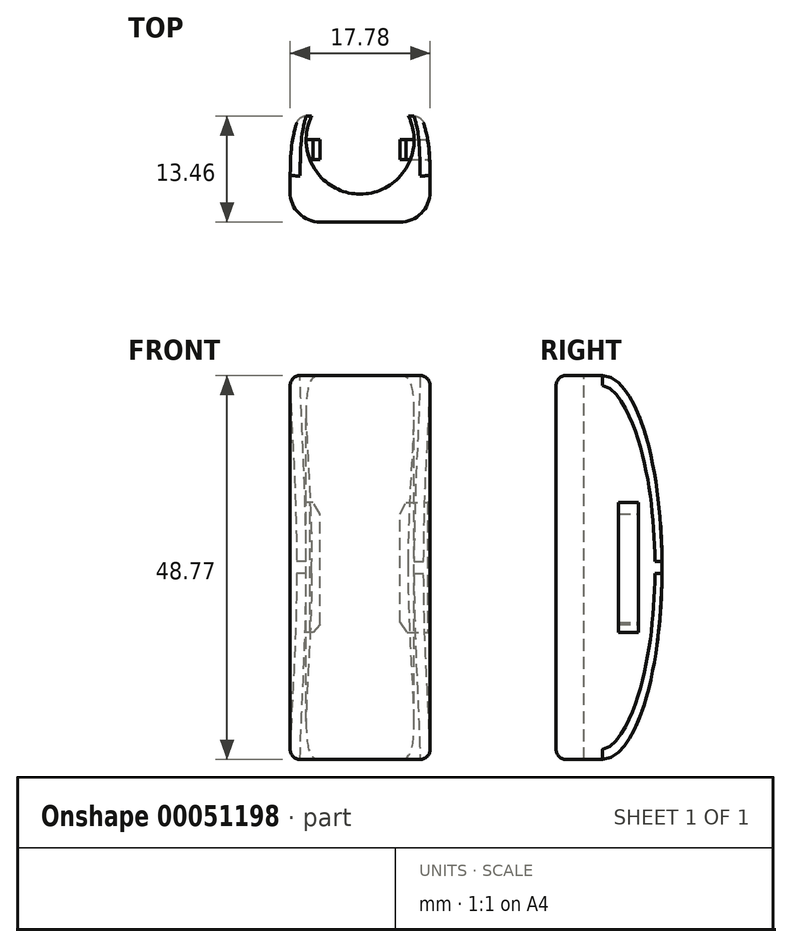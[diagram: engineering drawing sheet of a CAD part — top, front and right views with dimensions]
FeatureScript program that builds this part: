
annotation { "Feature Type Name" : "Feature", "Feature Type Description" : "" }
export const myFeature = defineFeature(function(context is Context, id is Id, definition is map)
    precondition{}
    {
        {
            var Q0;
            Q0=qCreatedBy(makeId("Top.planeOp"),FACE);
            var sketch = newSketch(context, id + "F0", { "sketchPlane" : qUnion([Q0])});
            skLineSegment(sketch, "E0.bottom", {"start": v(-25.3, 22.65) * mm, "end": v(-7.52, 22.65) * mm});
            skLineSegment(sketch, "E0.top", {"start": v(-25.3, 9.19) * mm, "end": v(-7.52, 9.19) * mm});
            skLineSegment(sketch, "E0.left", {"start": v(-25.3, 22.65) * mm, "end": v(-25.3, 9.19) * mm});
            skLineSegment(sketch, "E0.right", {"start": v(-7.52, 22.65) * mm, "end": v(-7.52, 9.19) * mm});
            skSolve(sketch);
        }
        {
            var Q0;
            Q0=makeQuery(id+"F0.imprint","IMPRINT",FACE,{"disambiguationData":[TD([[makeQuery(id+"F0.imprint","IMPRINT",EDGE,{"derivedFrom":sQuery(id+"F0.wireOp",EDGE,"E0.bottom")}),-1.0]])]});
            extrude(context, id + "F1", {"entities" : qUnion([Q0]), "depth" : 48.77 * mm});
        }
        {
            var Q0;
            Q0=makeQuery(id+"F1.opExtrude","CAP_FACE",FACE,{"disambiguationData":[OSD([sQuery(id+"F0.wireOp",EDGE,"E0.bottom"),sQuery(id+"F0.wireOp",EDGE,"E0.top"),sQuery(id+"F0.wireOp",EDGE,"E0.left"),sQuery(id+"F0.wireOp",EDGE,"E0.right")])],"isStart":false});
            var sketch = newSketch(context, id + "F2", { "sketchPlane" : qUnion([Q0])});
            skCircle(sketch, "E1", {"center": v(-16.41, 19.6) * mm, "radius": 6.86 * mm});
            skSolve(sketch);
        }
        {
            var Q0;
            {var subQ0=sQuery(id+"F2.wireOp",EDGE,"E1");var subQ1=makeQuery(id+"F1.opExtrude","CAP_EDGE",EDGE,{"disambiguationData":[OSD([sQuery(id+"F0.wireOp",EDGE,"E0.bottom")])],"isStart":false});var subQ2=makeQuery(id+"F2.imprint","INTERSECT",VERTEX,{"disambiguationData":[OD(0.0)],"derivedFrom":[subQ1,subQ0]});Q0=makeQuery(id+"F2.imprint","IMPRINT",FACE,{"disambiguationData":[TD([[makeQuery(id+"F2.imprint","IMPRINT",EDGE,{"disambiguationData":[TD([[subQ2,1.0]])],"derivedFrom":subQ0}),1.0]])]});}
            var Q1;
            {var subQ0=sQuery(id+"F2.wireOp",EDGE,"E1");var subQ1=makeQuery(id+"F1.opExtrude","CAP_EDGE",EDGE,{"disambiguationData":[OSD([sQuery(id+"F0.wireOp",EDGE,"E0.bottom")])],"isStart":false});var subQ2=makeQuery(id+"F2.imprint","INTERSECT",VERTEX,{"disambiguationData":[OD(0.0)],"derivedFrom":[subQ1,subQ0]});Q1=makeQuery(id+"F2.imprint","IMPRINT",FACE,{"disambiguationData":[TD([[makeQuery(id+"F2.imprint","IMPRINT",EDGE,{"disambiguationData":[TD([[subQ2,-1.0]])],"derivedFrom":subQ0}),1.0]])]});}
            extrude(context, id + "F3", {"entities" : qUnion([Q0, Q1]), "operationType" : NewBodyOperationType.REMOVE, "oppositeDirection" : true, "depth" : 127 * mm});
        }
        {
            var Q0;
            Q0=makeQuery(id+"F1.opExtrude","SWEPT_FACE",FACE,{"disambiguationData":[OSD([sQuery(id+"F0.wireOp",EDGE,"E0.left")])]});
            var sketch = newSketch(context, id + "F4", { "sketchPlane" : qUnion([Q0])});
            skLineSegment(sketch, "E2.bottom", {"start": v(-19.66, 16.13) * mm, "end": v(-17.12, 16.13) * mm});
            skLineSegment(sketch, "E2.top", {"start": v(-19.66, 32.64) * mm, "end": v(-17.12, 32.64) * mm});
            skLineSegment(sketch, "E2.left", {"start": v(-19.66, 16.13) * mm, "end": v(-19.66, 32.64) * mm});
            skLineSegment(sketch, "E2.right", {"start": v(-17.12, 16.13) * mm, "end": v(-17.12, 32.64) * mm});
            skSolve(sketch);
        }
        {
            var Q0;
            Q0=makeQuery(id+"F4.imprint","IMPRINT",FACE,{"disambiguationData":[TD([[makeQuery(id+"F4.imprint","IMPRINT",EDGE,{"derivedFrom":sQuery(id+"F4.wireOp",EDGE,"E2.bottom")}),1.0]])]});
            extrude(context, id + "F5", {"entities" : qUnion([Q0]), "operationType" : NewBodyOperationType.ADD, "oppositeDirection" : true, "depth" : 3.8 * mm});
        }
        {
            var Q0;
            Q0=makeQuery(id+"F1.opExtrude","CAP_FACE",FACE,{"disambiguationData":[OSD([sQuery(id+"F0.wireOp",EDGE,"E0.bottom"),sQuery(id+"F0.wireOp",EDGE,"E0.top"),sQuery(id+"F0.wireOp",EDGE,"E0.left"),sQuery(id+"F0.wireOp",EDGE,"E0.right")])],"isStart":false});
            var sketch = newSketch(context, id + "F6", { "sketchPlane" : qUnion([Q0])});
            skFitSpline(sketch, "E3", {"points": [v(-25.3, 12.21) * mm, v(-25.07, 19.12) * mm, v(-24.21, 22.65) * mm], "startDerivative": vector(-0.07, 12.93) * mm, "endDerivative": vector(2.38, 7.66) * mm});
            skFitSpline(sketch, "E4.MirrorCS", {"points": [v(-7.52, 12.21) * mm, v(-7.76, 19.12) * mm, v(-8.61, 22.65) * mm], "startDerivative": vector(0.07, 12.93) * mm, "endDerivative": vector(-2.38, 7.66) * mm});
            skSolve(sketch);
        }
        {
            var Q0;
            {var subQ0=sQuery(id+"F6.wireOp",EDGE,"fc3628cf-69c2-4551-9983-d84b999a87e0");Q0=makeQuery(id+"F6.imprint","IMPRINT",FACE,{"disambiguationData":[TD([[makeQuery(id+"F6.imprint","IMPRINT",EDGE,{"derivedFrom":subQ0}),1.0]])]});}
            var Q1;
            {var subQ0=sQuery(id+"F6.wireOp",EDGE,"20fc23eb-cc5c-43b9-b7d9-6a3f5bb52c0f0.MirrorCS");Q1=makeQuery(id+"F6.imprint","IMPRINT",FACE,{"disambiguationData":[TD([[makeQuery(id+"F6.imprint","IMPRINT",EDGE,{"derivedFrom":subQ0}),-1.0]])]});}
            var Q2;
            {var subQ0=sQuery(id+"F6.wireOp",EDGE,"E3");var subQ2=sQuery(id+"F0.wireOp",EDGE,"E0.left");var subQ5=makeQuery(id+"F1.opExtrude","CAP_EDGE",EDGE,{"disambiguationData":[OSD([subQ2])],"isStart":false});var subQ6=makeQuery(id+"F6.imprint","INTERSECT",VERTEX,{"disambiguationData":[OD(1.0)],"derivedFrom":[subQ5,subQ0]});Q2=makeQuery(id+"F6.imprint","IMPRINT",FACE,{"disambiguationData":[TD([[makeQuery(id+"F6.imprint","IMPRINT",EDGE,{"disambiguationData":[TD([[subQ6,-1.0]])],"derivedFrom":subQ0}),1.0]])]});}
            var Q3;
            {var subQ0=sQuery(id+"F6.wireOp",EDGE,"E4.MirrorCS");var subQ2=sQuery(id+"F0.wireOp",EDGE,"E0.right");var subQ5=makeQuery(id+"F1.opExtrude","CAP_EDGE",EDGE,{"disambiguationData":[OSD([subQ2])],"isStart":false});var subQ6=makeQuery(id+"F6.imprint","INTERSECT",VERTEX,{"disambiguationData":[OD(1.0)],"derivedFrom":[subQ5,subQ0]});Q3=makeQuery(id+"F6.imprint","IMPRINT",FACE,{"disambiguationData":[TD([[makeQuery(id+"F6.imprint","IMPRINT",EDGE,{"disambiguationData":[TD([[subQ6,-1.0]])],"derivedFrom":subQ0}),-1.0]])]});}
            extrude(context, id + "F7", {"entities" : qUnion([Q0, Q1, Q2, Q3]), "operationType" : NewBodyOperationType.REMOVE, "oppositeDirection" : true, "depth" : 76.2 * mm});
        }
        {
            var Q0;
            Q0=makeQuery(id+"F1.opExtrude","SWEPT_EDGE",EDGE,{"disambiguationData":[OSD([sQuery(id+"F0.wireOp",EDGE,"E0.top"),sQuery(id+"F0.wireOp",EDGE,"E0.right")])]});
            var Q1;
            Q1=makeQuery(id+"F1.opExtrude","SWEPT_EDGE",EDGE,{"disambiguationData":[OSD([sQuery(id+"F0.wireOp",EDGE,"E0.top"),sQuery(id+"F0.wireOp",EDGE,"E0.left")])]});
            fillet(context, id + "F8", {"entities" : qUnion([Q0, Q1]), "radius" : 3.8 * mm, "tangentPropagation" : true, "allowEdgeOverflow" : false});
        }
        {
            var Q0;
            Q0=makeQuery(id+"F1.opExtrude","SWEPT_FACE",FACE,{"disambiguationData":[OSD([sQuery(id+"F0.wireOp",EDGE,"E0.left")])]});
            var sketch = newSketch(context, id + "F9", { "sketchPlane" : qUnion([Q0])});
            skEllipticalArc(sketch, "E5", {});
            skLineSegment(sketch, "E6", {"start": v(-15.06, 0) * mm, "end": v(-22.79, -10.05) * mm});
            skLineSegment(sketch, "E7", {"start": v(-22.79, -10.05) * mm, "end": v(-30.31, 18.86) * mm});
            skLineSegment(sketch, "E8", {"start": v(-30.31, 18.86) * mm, "end": v(-22.65, 24.38) * mm});
            skLineSegment(sketch, "E9", {"start": v(-22.65, 24.38) * mm, "end": v(-30.46, 41.8) * mm});
            skLineSegment(sketch, "E10", {"start": v(-30.46, 41.8) * mm, "end": v(-18.14, 61.05) * mm});
            skLineSegment(sketch, "E11", {"start": v(-18.14, 61.05) * mm, "end": v(-15.06, 48.77) * mm});
            const initialGuessF9  = {"E5": [-0.015061341374097393, 0.024384, 0, 1, 0.024384, 0.0075914439429358585, 0, 3.141592653589793]};
            skSetInitialGuess(sketch, initialGuessF9);
            skSolve(sketch);
        }
        {
            var Q0;
            {var subQ0=sQuery(id+"F9.wireOp",EDGE,"E6");Q0=makeQuery(id+"F9.imprint","IMPRINT",FACE,{"disambiguationData":[TD([[makeQuery(id+"F9.imprint","IMPRINT",EDGE,{"derivedFrom":subQ0}),-1.0]])]});}
            var Q1;
            {var subQ3=sQuery(id+"F9.wireOp",EDGE,"E9");Q1=makeQuery(id+"F9.imprint","IMPRINT",FACE,{"disambiguationData":[TD([[makeQuery(id+"F9.imprint","IMPRINT",EDGE,{"derivedFrom":subQ3}),-1.0]])]});}
            extrude(context, id + "F10", {"entities" : qUnion([Q0, Q1]), "operationType" : NewBodyOperationType.REMOVE, "oppositeDirection" : true, "depth" : 25.4 * mm});
        }
        {
            var Q0;
            {var subQ0=sQuery(id+"F9.wireOp",EDGE,"E5");var subQ2=sQuery(id+"F6.wireOp",EDGE,"E3");Q0=makeQuery(id+"F10.boolean.opBoolean","INTERSECT",EDGE,{"derivedFrom":[makeQuery(id+"F7.boolean.opBoolean","COPY",FACE,{"derivedFrom":makeQuery(id+"F7.opExtrude","SWEPT_FACE",FACE,{"disambiguationData":[OSD([subQ2])]})}),makeQuery(id+"F10.opExtrude","SWEPT_FACE",FACE,{"disambiguationData":[OSD([subQ0]),TDD([makeQuery(id+"F9.imprint","IMPRINT",EDGE,{"disambiguationData":[TD([[makeQuery(id+"F9.imprint","INTERSECT",VERTEX,{"derivedFrom":[subQ0,sQuery(id+"F9.wireOp",EDGE,"E8"),sQuery(id+"F9.wireOp",EDGE,"E9")]}),1.0]])],"derivedFrom":subQ0})])]})]});}
            var Q1;
            {var subQ0=sQuery(id+"F9.wireOp",EDGE,"E5");var subQ2=sQuery(id+"F6.wireOp",EDGE,"E3");Q1=makeQuery(id+"F10.boolean.opBoolean","INTERSECT",EDGE,{"derivedFrom":[makeQuery(id+"F7.boolean.opBoolean","COPY",FACE,{"derivedFrom":makeQuery(id+"F7.opExtrude","SWEPT_FACE",FACE,{"disambiguationData":[OSD([subQ2])]})}),makeQuery(id+"F10.opExtrude","SWEPT_FACE",FACE,{"disambiguationData":[OSD([subQ0]),TDD([makeQuery(id+"F9.imprint","IMPRINT",EDGE,{"disambiguationData":[TD([[makeQuery(id+"F9.imprint","INTERSECT",VERTEX,{"derivedFrom":[subQ0,sQuery(id+"F9.wireOp",EDGE,"E8"),sQuery(id+"F9.wireOp",EDGE,"E9")]}),-1.0]])],"derivedFrom":subQ0})])]})]});}
            var Q2;
            Q2=makeQuery(id+"F7.boolean.opBoolean","COPY",EDGE,{"derivedFrom":makeQuery(id+"F7.opExtrude","SWEPT_EDGE",EDGE,{"disambiguationData":[OSD([sQuery(id+"F0.wireOp",EDGE,"E0.bottom"),sQuery(id+"F6.wireOp",EDGE,"E3")])]})});
            var Q3;
            {var subQ0=sQuery(id+"F9.wireOp",EDGE,"E5");Q3=makeQuery(id+"F10.boolean.opBoolean","INTERSECT",EDGE,{"derivedFrom":[makeQuery(id+"F7.boolean.opBoolean","COPY",FACE,{"derivedFrom":makeQuery(id+"F7.opExtrude","SWEPT_FACE",FACE,{"disambiguationData":[OSD([sQuery(id+"F6.wireOp",EDGE,"E4.MirrorCS")])]})}),makeQuery(id+"F10.opExtrude","SWEPT_FACE",FACE,{"disambiguationData":[OSD([subQ0]),TDD([makeQuery(id+"F9.imprint","IMPRINT",EDGE,{"disambiguationData":[TD([[makeQuery(id+"F9.imprint","INTERSECT",VERTEX,{"derivedFrom":[subQ0,sQuery(id+"F9.wireOp",EDGE,"E8"),sQuery(id+"F9.wireOp",EDGE,"E9")]}),1.0]])],"derivedFrom":subQ0})])]})]});}
            var Q4;
            Q4=makeQuery(id+"F7.boolean.opBoolean","COPY",EDGE,{"derivedFrom":makeQuery(id+"F7.opExtrude","SWEPT_EDGE",EDGE,{"disambiguationData":[OSD([sQuery(id+"F0.wireOp",EDGE,"E0.bottom"),sQuery(id+"F6.wireOp",EDGE,"E4.MirrorCS")])]})});
            var Q5;
            {var subQ0=sQuery(id+"F9.wireOp",EDGE,"E5");Q5=makeQuery(id+"F10.boolean.opBoolean","INTERSECT",EDGE,{"derivedFrom":[makeQuery(id+"F7.boolean.opBoolean","COPY",FACE,{"derivedFrom":makeQuery(id+"F7.opExtrude","SWEPT_FACE",FACE,{"disambiguationData":[OSD([sQuery(id+"F6.wireOp",EDGE,"E4.MirrorCS")])]})}),makeQuery(id+"F10.opExtrude","SWEPT_FACE",FACE,{"disambiguationData":[OSD([subQ0]),TDD([makeQuery(id+"F9.imprint","IMPRINT",EDGE,{"disambiguationData":[TD([[makeQuery(id+"F9.imprint","INTERSECT",VERTEX,{"derivedFrom":[subQ0,sQuery(id+"F9.wireOp",EDGE,"E8"),sQuery(id+"F9.wireOp",EDGE,"E9")]}),-1.0]])],"derivedFrom":subQ0})])]})]});}
            fillet(context, id + "F11", {"entities" : qUnion([Q0, Q1, Q2, Q3, Q4, Q5]), "radius" : 1.27 * mm, "tangentPropagation" : true, "allowEdgeOverflow" : false});
        }
        {
            var Q0;
            Q0=makeQuery(id+"F1.opExtrude","CAP_EDGE",EDGE,{"disambiguationData":[OSD([sQuery(id+"F0.wireOp",EDGE,"E0.top")])],"isStart":false});
            var Q1;
            {var subQ0=sQuery(id+"F0.wireOp",EDGE,"E0.left");var subQ1=sQuery(id+"F0.wireOp",EDGE,"E0.top");Q1=makeQuery(id+"F8.opFillet","BLEND_EDGE",EDGE,{"blendedFrom":[makeQuery(id+"F1.opExtrude","SWEPT_EDGE",EDGE,{"disambiguationData":[OSD([subQ1,subQ0])]}),makeQuery(id+"F1.opExtrude","CAP_FACE",FACE,{"disambiguationData":[OSD([sQuery(id+"F0.wireOp",EDGE,"E0.bottom"),subQ1,subQ0,sQuery(id+"F0.wireOp",EDGE,"E0.right")])],"isStart":false})],"blendedInto":[makeQuery(id+"F1.opExtrude","CAP_FACE",FACE,{"disambiguationData":[OSD([sQuery(id+"F0.wireOp",EDGE,"E0.bottom"),subQ1,subQ0,sQuery(id+"F0.wireOp",EDGE,"E0.right")])],"isStart":false})]});}
            var Q2;
            {var subQ0=sQuery(id+"F0.wireOp",EDGE,"E0.left");var subQ1=sQuery(id+"F9.wireOp",EDGE,"E5");var subQ2=sQuery(id+"F6.wireOp",EDGE,"E3");Q2=makeQuery(id+"F11.opFillet","BLEND_EDGE",EDGE,{"blendedFrom":[makeQuery(id+"F10.boolean.opBoolean","INTERSECT",EDGE,{"derivedFrom":[makeQuery(id+"F7.boolean.opBoolean","COPY",FACE,{"derivedFrom":makeQuery(id+"F7.opExtrude","SWEPT_FACE",FACE,{"disambiguationData":[OSD([subQ2])]})}),makeQuery(id+"F10.opExtrude","SWEPT_FACE",FACE,{"disambiguationData":[OSD([subQ1]),TDD([makeQuery(id+"F9.imprint","IMPRINT",EDGE,{"disambiguationData":[TD([[makeQuery(id+"F9.imprint","INTERSECT",VERTEX,{"derivedFrom":[subQ1,sQuery(id+"F9.wireOp",EDGE,"E8"),sQuery(id+"F9.wireOp",EDGE,"E9")]}),1.0]])],"derivedFrom":subQ1})])]})]}),makeQuery(id+"F8.opFillet","BLEND_FACE",FACE,{"disambiguationData":[OSD([sQuery(id+"F0.wireOp",EDGE,"E0.top"),subQ0])]})],"blendedInto":[makeQuery(id+"F8.opFillet","BLEND_FACE",FACE,{"disambiguationData":[OSD([sQuery(id+"F0.wireOp",EDGE,"E0.top"),subQ0])]})]});}
            var Q3;
            {var subQ0=sQuery(id+"F0.wireOp",EDGE,"E0.right");var subQ1=sQuery(id+"F0.wireOp",EDGE,"E0.top");Q3=makeQuery(id+"F8.opFillet","BLEND_EDGE",EDGE,{"blendedFrom":[makeQuery(id+"F1.opExtrude","SWEPT_EDGE",EDGE,{"disambiguationData":[OSD([subQ1,subQ0])]}),makeQuery(id+"F1.opExtrude","CAP_FACE",FACE,{"disambiguationData":[OSD([sQuery(id+"F0.wireOp",EDGE,"E0.bottom"),subQ1,sQuery(id+"F0.wireOp",EDGE,"E0.left"),subQ0])],"isStart":false})],"blendedInto":[makeQuery(id+"F1.opExtrude","CAP_FACE",FACE,{"disambiguationData":[OSD([sQuery(id+"F0.wireOp",EDGE,"E0.bottom"),subQ1,sQuery(id+"F0.wireOp",EDGE,"E0.left"),subQ0])],"isStart":false})]});}
            var Q4;
            {var subQ0=sQuery(id+"F9.wireOp",EDGE,"E5");Q4=makeQuery(id+"F11.opFillet","BLEND_EDGE",EDGE,{"blendedFrom":[makeQuery(id+"F10.boolean.opBoolean","INTERSECT",EDGE,{"derivedFrom":[makeQuery(id+"F7.boolean.opBoolean","COPY",FACE,{"derivedFrom":makeQuery(id+"F7.opExtrude","SWEPT_FACE",FACE,{"disambiguationData":[OSD([sQuery(id+"F6.wireOp",EDGE,"E4.MirrorCS")])]})}),makeQuery(id+"F10.opExtrude","SWEPT_FACE",FACE,{"disambiguationData":[OSD([subQ0]),TDD([makeQuery(id+"F9.imprint","IMPRINT",EDGE,{"disambiguationData":[TD([[makeQuery(id+"F9.imprint","INTERSECT",VERTEX,{"derivedFrom":[subQ0,sQuery(id+"F9.wireOp",EDGE,"E8"),sQuery(id+"F9.wireOp",EDGE,"E9")]}),1.0]])],"derivedFrom":subQ0})])]})]}),makeQuery(id+"F8.opFillet","BLEND_FACE",FACE,{"disambiguationData":[OSD([sQuery(id+"F0.wireOp",EDGE,"E0.top"),sQuery(id+"F0.wireOp",EDGE,"E0.right")])]})],"blendedInto":[makeQuery(id+"F8.opFillet","BLEND_FACE",FACE,{"disambiguationData":[OSD([sQuery(id+"F0.wireOp",EDGE,"E0.top"),sQuery(id+"F0.wireOp",EDGE,"E0.right")])]})]});}
            fillet(context, id + "F12", {"entities" : qUnion([Q0, Q1, Q2, Q3, Q4]), "radius" : 1.27 * mm, "tangentPropagation" : true, "allowEdgeOverflow" : false});
        }
        {
            var Q0;
            Q0=makeQuery(id+"F5.opExtrude","SWEPT_FACE",FACE,{"disambiguationData":[OSD([sQuery(id+"F4.wireOp",EDGE,"E2.left")])]});
            var sketch = newSketch(context, id + "F13", { "sketchPlane" : qUnion([Q0])});
            skLineSegment(sketch, "E12", {"start": v(21.5, 31.17) * mm, "end": v(22.38, 32.64) * mm});
            skLineSegment(sketch, "E13", {"start": v(21.5, 17.18) * mm, "end": v(22.38, 16.13) * mm});
            skSolve(sketch);
        }
        {
            var Q0;
            {var subQ0=sQuery(id+"F13.wireOp",EDGE,"E12");Q0=makeQuery(id+"F13.imprint","IMPRINT",FACE,{"disambiguationData":[TD([[makeQuery(id+"F13.imprint","IMPRINT",EDGE,{"derivedFrom":subQ0}),1.0]])]});}
            var Q1;
            {var subQ0=sQuery(id+"F13.wireOp",EDGE,"E13");Q1=makeQuery(id+"F13.imprint","IMPRINT",FACE,{"disambiguationData":[TD([[makeQuery(id+"F13.imprint","IMPRINT",EDGE,{"derivedFrom":subQ0}),-1.0]])]});}
            extrude(context, id + "F14", {"entities" : qUnion([Q0, Q1]), "operationType" : NewBodyOperationType.REMOVE, "oppositeDirection" : true, "depth" : 2.54 * mm});
        }
        {
            var Q0;
            Q0=makeQuery(id+"F1.opExtrude","SWEPT_FACE",FACE,{"disambiguationData":[OSD([sQuery(id+"F0.wireOp",EDGE,"E0.right")])]});
            var sketch = newSketch(context, id + "F15", { "sketchPlane" : qUnion([Q0])});
            skLineSegment(sketch, "E14.left", {"start": v(17.11, 16.13) * mm, "end": v(17.11, 32.64) * mm});
            skLineSegment(sketch, "E14.right", {"start": v(19.65, 16.13) * mm, "end": v(19.65, 32.64) * mm});
            skLineSegment(sketch, "E14.bottom", {"start": v(17.11, 16.13) * mm, "end": v(19.65, 16.13) * mm});
            skLineSegment(sketch, "E14.top", {"start": v(17.11, 32.64) * mm, "end": v(19.65, 32.64) * mm});
            skSolve(sketch);
        }
        {
            var Q0;
            Q0 = qSketchRegion(id + "F15", true);
            extrude(context, id + "F16", {"entities" : qUnion([Q0]), "oppositeDirection" : true, "depth" : 3.8 * mm});
        }
        {
            var Q0;
            Q0=makeQuery(id+"F16.opExtrude","SWEPT_FACE",FACE,{"disambiguationData":[OSD([sQuery(id+"F15.wireOp",EDGE,"E14.right")])]});
            var sketch = newSketch(context, id + "F17", { "sketchPlane" : qUnion([Q0])});
            skLineSegment(sketch, "E15", {"start": v(11.33, 31.2) * mm, "end": v(10.6, 32.64) * mm});
            skLineSegment(sketch, "E16", {"start": v(11.33, 17.43) * mm, "end": v(10.47, 16.13) * mm});
            skSolve(sketch);
        }
        {
            var Q0;
            {var subQ0=sQuery(id+"F17.wireOp",EDGE,"E15");Q0=makeQuery(id+"F17.imprint","IMPRINT",FACE,{"disambiguationData":[TD([[makeQuery(id+"F17.imprint","IMPRINT",EDGE,{"derivedFrom":subQ0}),-1.0]])]});}
            var Q1;
            {var subQ0=sQuery(id+"F17.wireOp",EDGE,"E16");Q1=makeQuery(id+"F17.imprint","IMPRINT",FACE,{"disambiguationData":[TD([[makeQuery(id+"F17.imprint","IMPRINT",EDGE,{"derivedFrom":subQ0}),1.0]])]});}
            extrude(context, id + "F18", {"entities" : qUnion([Q0, Q1]), "operationType" : NewBodyOperationType.REMOVE, "oppositeDirection" : true, "depth" : 2.54 * mm});
        }
        {
            var Q0;
            Q0=makeQuery(id+"F16.opExtrude","SWEPT_FACE",FACE,{"disambiguationData":[OSD([sQuery(id+"F15.wireOp",EDGE,"E14.bottom")])]});
            var sketch = newSketch(context, id + "F19", { "sketchPlane" : qUnion([Q0])});
            skFitSpline(sketch, "E17", {"points": [v(-7.57, -17.11) * mm, v(-7.67, -18.61) * mm, v(-7.82, -19.65) * mm], "startDerivative": vector(-0.13, -2.86) * mm, "endDerivative": vector(-0.38, -2.2) * mm});
            skLineSegment(sketch, "E18", {"start": v(-7.57, -17.11) * mm, "end": v(-7.06, -17.11) * mm});
            skLineSegment(sketch, "E19", {"start": v(-7.06, -17.11) * mm, "end": v(-7.36, -19.76) * mm});
            skLineSegment(sketch, "E20", {"start": v(-7.36, -19.76) * mm, "end": v(-7.82, -19.65) * mm});
            skSolve(sketch);
        }
        {
            var Q0;
            {var subQ0=sQuery(id+"F19.wireOp",EDGE,"E17");Q0=makeQuery(id+"F19.imprint","IMPRINT",FACE,{"disambiguationData":[TD([[makeQuery(id+"F19.imprint","IMPRINT",EDGE,{"derivedFrom":subQ0}),1.0]])]});}
            extrude(context, id + "F20", {"entities" : qUnion([Q0]), "operationType" : NewBodyOperationType.REMOVE, "oppositeDirection" : true, "depth" : 25.4 * mm});
        }
    });
